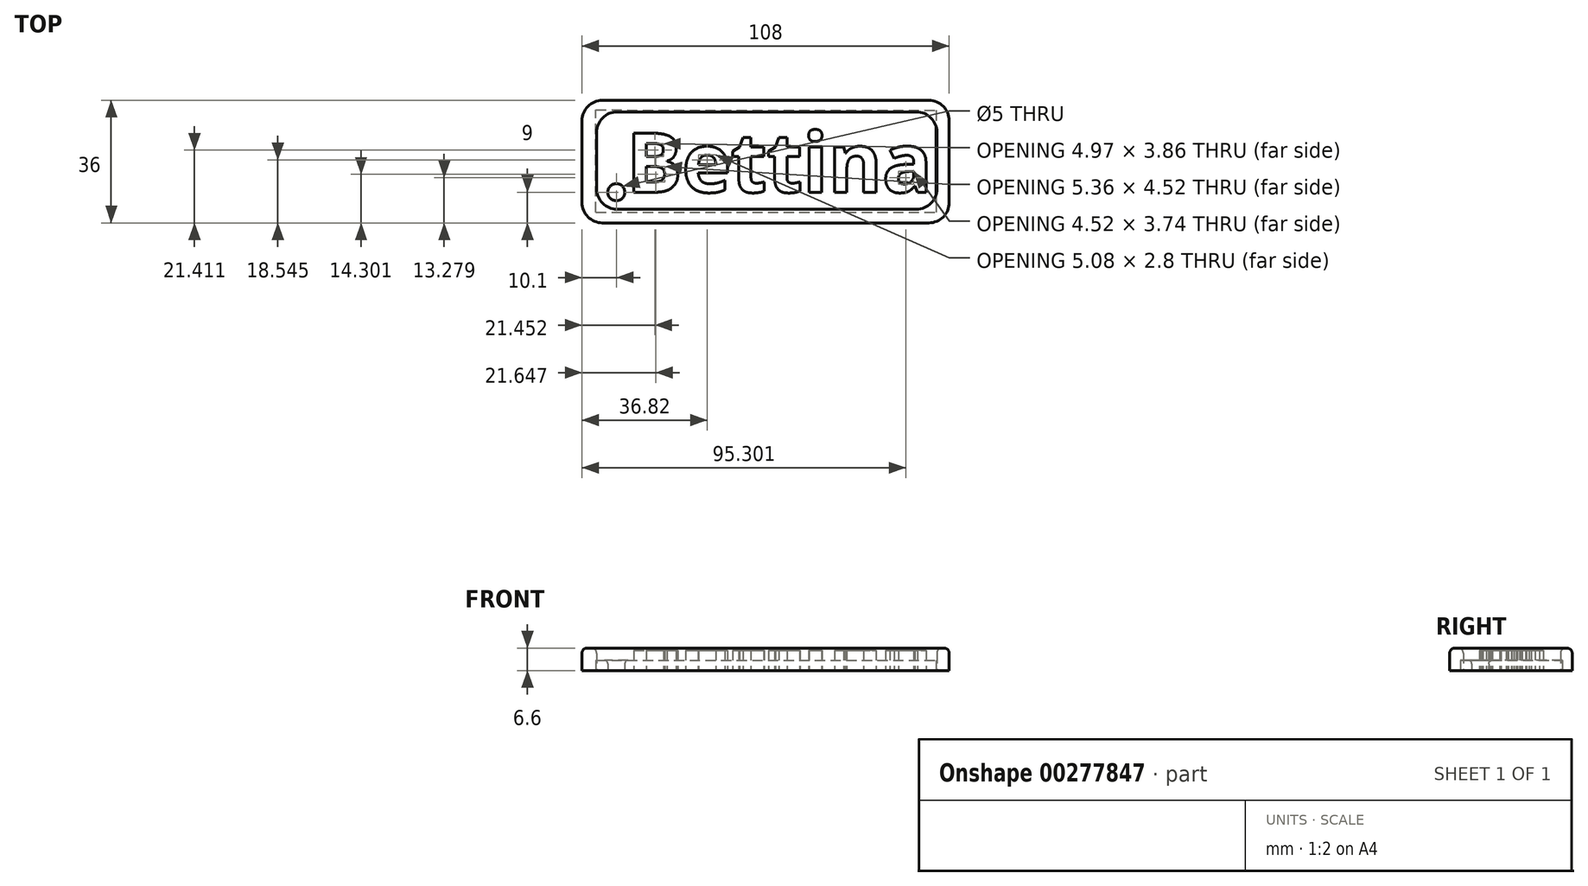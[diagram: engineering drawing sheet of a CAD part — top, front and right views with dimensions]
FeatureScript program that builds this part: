
annotation { "Feature Type Name" : "Feature", "Feature Type Description" : "" }
export const myFeature = defineFeature(function(context is Context, id is Id, definition is map)
    precondition{}
    {
        {
            var Q0;
            Q0=qCreatedBy(makeId("Top.planeOp"),FACE);
            var sketch = newSketch(context, id + "F0", { "sketchPlane" : qUnion([Q0])});
            skText(sketch, "E0", { "text": "Bettina", "fontName": "OpenSans-Bold.ttf"});
            const initialGuessF0  = {"E0": [0, 0, 1, 0, 0.02334]};
            skSetInitialGuess(sketch, initialGuessF0);
            skSolve(sketch);
        }
        {
            var Q0;
            Q0 = qSketchRegion(id + "F0", true);
            extrude(context, id + "F1", {"entities" : qUnion([Q0]), "depth" : 8 * mm});
        }
        {
            var Q0;
            Q0=makeQuery(id+"F1.opExtrude","SWEPT_BODY",BODY,{"disambiguationData":[OSD([sQuery(id+"F0.wireOp",EDGE,"E0.sketch_text.stroke-0"),sQuery(id+"F0.wireOp",EDGE,"E0.sketch_text.stroke-1"),sQuery(id+"F0.wireOp",EDGE,"E0.sketch_text.stroke-2"),sQuery(id+"F0.wireOp",EDGE,"E0.sketch_text.stroke-3"),sQuery(id+"F0.wireOp",EDGE,"E0.sketch_text.stroke-4"),sQuery(id+"F0.wireOp",EDGE,"E0.sketch_text.stroke-5"),sQuery(id+"F0.wireOp",EDGE,"E0.sketch_text.stroke-6"),sQuery(id+"F0.wireOp",EDGE,"E0.sketch_text.stroke-7"),sQuery(id+"F0.wireOp",EDGE,"E0.sketch_text.stroke-8"),sQuery(id+"F0.wireOp",EDGE,"E0.sketch_text.stroke-9"),sQuery(id+"F0.wireOp",EDGE,"E0.sketch_text.stroke-10"),sQuery(id+"F0.wireOp",EDGE,"E0.sketch_text.stroke-11"),sQuery(id+"F0.wireOp",EDGE,"E0.sketch_text.stroke-12"),sQuery(id+"F0.wireOp",EDGE,"E0.sketch_text.stroke-13"),sQuery(id+"F0.wireOp",EDGE,"E0.sketch_text.stroke-14"),sQuery(id+"F0.wireOp",EDGE,"E0.sketch_text.stroke-15"),sQuery(id+"F0.wireOp",EDGE,"E0.sketch_text.stroke-16"),sQuery(id+"F0.wireOp",EDGE,"E0.sketch_text.stroke-17"),sQuery(id+"F0.wireOp",EDGE,"E0.sketch_text.stroke-18"),sQuery(id+"F0.wireOp",EDGE,"E0.sketch_text.stroke-19"),sQuery(id+"F0.wireOp",EDGE,"E0.sketch_text.stroke-20"),sQuery(id+"F0.wireOp",EDGE,"E0.sketch_text.stroke-21"),sQuery(id+"F0.wireOp",EDGE,"E0.sketch_text.stroke-22"),sQuery(id+"F0.wireOp",EDGE,"E0.sketch_text.stroke-23"),sQuery(id+"F0.wireOp",EDGE,"E0.sketch_text.stroke-24")])]});
            var Q1;
            Q1=makeQuery(id+"F1.opExtrude","SWEPT_BODY",BODY,{"disambiguationData":[OSD([sQuery(id+"F0.wireOp",EDGE,"E0.sketch_text.stroke-25"),sQuery(id+"F0.wireOp",EDGE,"E0.sketch_text.stroke-26"),sQuery(id+"F0.wireOp",EDGE,"E0.sketch_text.stroke-27"),sQuery(id+"F0.wireOp",EDGE,"E0.sketch_text.stroke-28"),sQuery(id+"F0.wireOp",EDGE,"E0.sketch_text.stroke-29"),sQuery(id+"F0.wireOp",EDGE,"E0.sketch_text.stroke-30"),sQuery(id+"F0.wireOp",EDGE,"E0.sketch_text.stroke-31"),sQuery(id+"F0.wireOp",EDGE,"E0.sketch_text.stroke-32"),sQuery(id+"F0.wireOp",EDGE,"E0.sketch_text.stroke-33"),sQuery(id+"F0.wireOp",EDGE,"E0.sketch_text.stroke-34"),sQuery(id+"F0.wireOp",EDGE,"E0.sketch_text.stroke-35"),sQuery(id+"F0.wireOp",EDGE,"E0.sketch_text.stroke-36"),sQuery(id+"F0.wireOp",EDGE,"E0.sketch_text.stroke-37"),sQuery(id+"F0.wireOp",EDGE,"E0.sketch_text.stroke-38"),sQuery(id+"F0.wireOp",EDGE,"E0.sketch_text.stroke-39"),sQuery(id+"F0.wireOp",EDGE,"E0.sketch_text.stroke-40"),sQuery(id+"F0.wireOp",EDGE,"E0.sketch_text.stroke-41"),sQuery(id+"F0.wireOp",EDGE,"E0.sketch_text.stroke-42"),sQuery(id+"F0.wireOp",EDGE,"E0.sketch_text.stroke-43"),sQuery(id+"F0.wireOp",EDGE,"E0.sketch_text.stroke-44")])]});
            var Q2;
            Q2=makeQuery(id+"F1.opExtrude","SWEPT_BODY",BODY,{"disambiguationData":[OSD([sQuery(id+"F0.wireOp",EDGE,"E0.sketch_text.stroke-45"),sQuery(id+"F0.wireOp",EDGE,"E0.sketch_text.stroke-46"),sQuery(id+"F0.wireOp",EDGE,"E0.sketch_text.stroke-47"),sQuery(id+"F0.wireOp",EDGE,"E0.sketch_text.stroke-48"),sQuery(id+"F0.wireOp",EDGE,"E0.sketch_text.stroke-49"),sQuery(id+"F0.wireOp",EDGE,"E0.sketch_text.stroke-50"),sQuery(id+"F0.wireOp",EDGE,"E0.sketch_text.stroke-51"),sQuery(id+"F0.wireOp",EDGE,"E0.sketch_text.stroke-52"),sQuery(id+"F0.wireOp",EDGE,"E0.sketch_text.stroke-53"),sQuery(id+"F0.wireOp",EDGE,"E0.sketch_text.stroke-54"),sQuery(id+"F0.wireOp",EDGE,"E0.sketch_text.stroke-55"),sQuery(id+"F0.wireOp",EDGE,"E0.sketch_text.stroke-56"),sQuery(id+"F0.wireOp",EDGE,"E0.sketch_text.stroke-57"),sQuery(id+"F0.wireOp",EDGE,"E0.sketch_text.stroke-58"),sQuery(id+"F0.wireOp",EDGE,"E0.sketch_text.stroke-59"),sQuery(id+"F0.wireOp",EDGE,"E0.sketch_text.stroke-60"),sQuery(id+"F0.wireOp",EDGE,"E0.sketch_text.stroke-61"),sQuery(id+"F0.wireOp",EDGE,"E0.sketch_text.stroke-62")])]});
            var Q3;
            Q3=makeQuery(id+"F1.opExtrude","SWEPT_BODY",BODY,{"disambiguationData":[OSD([sQuery(id+"F0.wireOp",EDGE,"E0.sketch_text.stroke-63"),sQuery(id+"F0.wireOp",EDGE,"E0.sketch_text.stroke-64"),sQuery(id+"F0.wireOp",EDGE,"E0.sketch_text.stroke-65"),sQuery(id+"F0.wireOp",EDGE,"E0.sketch_text.stroke-66"),sQuery(id+"F0.wireOp",EDGE,"E0.sketch_text.stroke-67"),sQuery(id+"F0.wireOp",EDGE,"E0.sketch_text.stroke-68"),sQuery(id+"F0.wireOp",EDGE,"E0.sketch_text.stroke-69"),sQuery(id+"F0.wireOp",EDGE,"E0.sketch_text.stroke-70"),sQuery(id+"F0.wireOp",EDGE,"E0.sketch_text.stroke-71"),sQuery(id+"F0.wireOp",EDGE,"E0.sketch_text.stroke-72"),sQuery(id+"F0.wireOp",EDGE,"E0.sketch_text.stroke-73"),sQuery(id+"F0.wireOp",EDGE,"E0.sketch_text.stroke-74"),sQuery(id+"F0.wireOp",EDGE,"E0.sketch_text.stroke-75"),sQuery(id+"F0.wireOp",EDGE,"E0.sketch_text.stroke-76"),sQuery(id+"F0.wireOp",EDGE,"E0.sketch_text.stroke-77"),sQuery(id+"F0.wireOp",EDGE,"E0.sketch_text.stroke-78"),sQuery(id+"F0.wireOp",EDGE,"E0.sketch_text.stroke-79"),sQuery(id+"F0.wireOp",EDGE,"E0.sketch_text.stroke-80")])]});
            var Q4;
            Q4=makeQuery(id+"F1.opExtrude","SWEPT_BODY",BODY,{"disambiguationData":[OSD([sQuery(id+"F0.wireOp",EDGE,"E0.sketch_text.stroke-81"),sQuery(id+"F0.wireOp",EDGE,"E0.sketch_text.stroke-82"),sQuery(id+"F0.wireOp",EDGE,"E0.sketch_text.stroke-83"),sQuery(id+"F0.wireOp",EDGE,"E0.sketch_text.stroke-84"),sQuery(id+"F0.wireOp",EDGE,"E0.sketch_text.stroke-85")])]});
            var Q5;
            Q5=makeQuery(id+"F1.opExtrude","SWEPT_BODY",BODY,{"disambiguationData":[OSD([sQuery(id+"F0.wireOp",EDGE,"E0.sketch_text.stroke-86"),sQuery(id+"F0.wireOp",EDGE,"E0.sketch_text.stroke-87"),sQuery(id+"F0.wireOp",EDGE,"E0.sketch_text.stroke-88"),sQuery(id+"F0.wireOp",EDGE,"E0.sketch_text.stroke-89")])]});
            var Q6;
            Q6=makeQuery(id+"F1.opExtrude","SWEPT_BODY",BODY,{"disambiguationData":[OSD([sQuery(id+"F0.wireOp",EDGE,"E0.sketch_text.stroke-90"),sQuery(id+"F0.wireOp",EDGE,"E0.sketch_text.stroke-91"),sQuery(id+"F0.wireOp",EDGE,"E0.sketch_text.stroke-92"),sQuery(id+"F0.wireOp",EDGE,"E0.sketch_text.stroke-93"),sQuery(id+"F0.wireOp",EDGE,"E0.sketch_text.stroke-94"),sQuery(id+"F0.wireOp",EDGE,"E0.sketch_text.stroke-95"),sQuery(id+"F0.wireOp",EDGE,"E0.sketch_text.stroke-96"),sQuery(id+"F0.wireOp",EDGE,"E0.sketch_text.stroke-97"),sQuery(id+"F0.wireOp",EDGE,"E0.sketch_text.stroke-98"),sQuery(id+"F0.wireOp",EDGE,"E0.sketch_text.stroke-99"),sQuery(id+"F0.wireOp",EDGE,"E0.sketch_text.stroke-100"),sQuery(id+"F0.wireOp",EDGE,"E0.sketch_text.stroke-101"),sQuery(id+"F0.wireOp",EDGE,"E0.sketch_text.stroke-102"),sQuery(id+"F0.wireOp",EDGE,"E0.sketch_text.stroke-103"),sQuery(id+"F0.wireOp",EDGE,"E0.sketch_text.stroke-104"),sQuery(id+"F0.wireOp",EDGE,"E0.sketch_text.stroke-105"),sQuery(id+"F0.wireOp",EDGE,"E0.sketch_text.stroke-106")])]});
            var Q7;
            Q7=makeQuery(id+"F1.opExtrude","SWEPT_BODY",BODY,{"disambiguationData":[OSD([sQuery(id+"F0.wireOp",EDGE,"E0.sketch_text.stroke-107"),sQuery(id+"F0.wireOp",EDGE,"E0.sketch_text.stroke-108"),sQuery(id+"F0.wireOp",EDGE,"E0.sketch_text.stroke-109"),sQuery(id+"F0.wireOp",EDGE,"E0.sketch_text.stroke-110"),sQuery(id+"F0.wireOp",EDGE,"E0.sketch_text.stroke-111"),sQuery(id+"F0.wireOp",EDGE,"E0.sketch_text.stroke-112"),sQuery(id+"F0.wireOp",EDGE,"E0.sketch_text.stroke-113"),sQuery(id+"F0.wireOp",EDGE,"E0.sketch_text.stroke-114"),sQuery(id+"F0.wireOp",EDGE,"E0.sketch_text.stroke-115"),sQuery(id+"F0.wireOp",EDGE,"E0.sketch_text.stroke-116"),sQuery(id+"F0.wireOp",EDGE,"E0.sketch_text.stroke-117"),sQuery(id+"F0.wireOp",EDGE,"E0.sketch_text.stroke-118"),sQuery(id+"F0.wireOp",EDGE,"E0.sketch_text.stroke-119"),sQuery(id+"F0.wireOp",EDGE,"E0.sketch_text.stroke-120"),sQuery(id+"F0.wireOp",EDGE,"E0.sketch_text.stroke-121"),sQuery(id+"F0.wireOp",EDGE,"E0.sketch_text.stroke-122"),sQuery(id+"F0.wireOp",EDGE,"E0.sketch_text.stroke-123"),sQuery(id+"F0.wireOp",EDGE,"E0.sketch_text.stroke-124"),sQuery(id+"F0.wireOp",EDGE,"E0.sketch_text.stroke-125"),sQuery(id+"F0.wireOp",EDGE,"E0.sketch_text.stroke-126"),sQuery(id+"F0.wireOp",EDGE,"E0.sketch_text.stroke-127"),sQuery(id+"F0.wireOp",EDGE,"E0.sketch_text.stroke-128"),sQuery(id+"F0.wireOp",EDGE,"E0.sketch_text.stroke-129"),sQuery(id+"F0.wireOp",EDGE,"E0.sketch_text.stroke-130"),sQuery(id+"F0.wireOp",EDGE,"E0.sketch_text.stroke-131")])]});
            var Q8;
            Q8=qCreatedBy(makeId("Origin.pointOp"),VERTEX);
            transform(context, id + "F2", {"entities" : qUnion([Q0, Q1, Q2, Q3, Q4, Q5, Q6, Q7]), "transformType" : TransformType.SCALE_UNIFORMLY, "scale" : 0.75, "scalePoint" : qUnion([Q8]), "makeCopy" : false});
        }
        {
            var Q0;
            Q0=qCreatedBy(makeId("Top.planeOp"),FACE);
            var sketch = newSketch(context, id + "F3", { "sketchPlane" : qUnion([Q0])});
            skLineSegment(sketch, "E1", {"start": v(-4.79, -5) * mm, "end": v(95.21, -5) * mm});
            skLineSegment(sketch, "E2.bottom", {"start": v(-4.79, -5) * mm, "end": v(95.26, -5) * mm});
            skLineSegment(sketch, "E2.top", {"start": v(-4.79, 23.6) * mm, "end": v(95.26, 23.6) * mm});
            skLineSegment(sketch, "E2.left", {"start": v(-4.79, -5) * mm, "end": v(-4.79, 23.6) * mm});
            skLineSegment(sketch, "E2.right", {"start": v(95.26, -5) * mm, "end": v(95.26, 23.6) * mm});
            skLineSegment(sketch, "E3", {"start": v(-9.1, 27) * mm, "end": v(98.9, 27) * mm});
            skLineSegment(sketch, "E4", {"start": v(98.9, 27) * mm, "end": v(98.9, -9) * mm});
            skLineSegment(sketch, "E5", {"start": v(98.9, -9) * mm, "end": v(-9.1, -9) * mm});
            skLineSegment(sketch, "E6", {"start": v(-9.1, -9) * mm, "end": v(-9.1, 27) * mm});
            skSolve(sketch);
        }
        {
            var Q0;
            Q0 = qSketchRegion(id + "F3", true);
            extrude(context, id + "F4", {"entities" : qUnion([Q0]), "depth" : 6.6 * mm});
        }
        {
            var Q0;
            Q0=qCreatedBy(makeId("Top.planeOp"),FACE);
            var sketch = newSketch(context, id + "F5", { "sketchPlane" : qUnion([Q0])});
            skLineSegment(sketch, "E7", {"start": v(-5, -5.84) * mm, "end": v(-5, 24.16) * mm});
            skLineSegment(sketch, "E8", {"start": v(-5, 24.16) * mm, "end": v(95, 24.1) * mm});
            skLineSegment(sketch, "E9", {"start": v(95, 24.1) * mm, "end": v(94.98, -5.9) * mm});
            skLineSegment(sketch, "E10", {"start": v(-5, -5.84) * mm, "end": v(-5, -4) * mm});
            skLineSegment(sketch, "E11", {"start": v(-5, -5.84) * mm, "end": v(94.98, -5.9) * mm});
            skSolve(sketch);
        }
        {
            var Q0;
            Q0 = qSketchRegion(id + "F5", true);
            extrude(context, id + "F6", {"entities" : qUnion([Q0]), "depth" : 3 * mm});
        }
        {
            var Q0;
            Q0=makeQuery(id+"F4.opExtrude","SWEPT_EDGE",EDGE,{"disambiguationData":[OSD([sQuery(id+"F3.wireOp",EDGE,"E2.top"),sQuery(id+"F3.wireOp",EDGE,"E2.right")])]});
            var Q1;
            Q1=makeQuery(id+"F4.opExtrude","SWEPT_EDGE",EDGE,{"disambiguationData":[OSD([sQuery(id+"F3.wireOp",EDGE,"E2.bottom"),sQuery(id+"F3.wireOp",EDGE,"E2.right")])]});
            var Q2;
            Q2=makeQuery(id+"F4.opExtrude","SWEPT_EDGE",EDGE,{"disambiguationData":[OSD([sQuery(id+"F3.wireOp",EDGE,"E2.bottom"),sQuery(id+"F3.wireOp",EDGE,"E2.left")])]});
            var Q3;
            Q3=makeQuery(id+"F4.opExtrude","SWEPT_EDGE",EDGE,{"disambiguationData":[OSD([sQuery(id+"F3.wireOp",EDGE,"E2.top"),sQuery(id+"F3.wireOp",EDGE,"E2.left")])]});
            var Q4;
            Q4=makeQuery(id+"F4.opExtrude","SWEPT_EDGE",EDGE,{"disambiguationData":[OSD([sQuery(id+"F3.wireOp",EDGE,"E5"),sQuery(id+"F3.wireOp",EDGE,"E6")])]});
            var Q5;
            Q5=makeQuery(id+"F4.opExtrude","SWEPT_EDGE",EDGE,{"disambiguationData":[OSD([sQuery(id+"F3.wireOp",EDGE,"E3"),sQuery(id+"F3.wireOp",EDGE,"E6")])]});
            var Q6;
            Q6=makeQuery(id+"F4.opExtrude","SWEPT_EDGE",EDGE,{"disambiguationData":[OSD([sQuery(id+"F3.wireOp",EDGE,"E4"),sQuery(id+"F3.wireOp",EDGE,"E5")])]});
            var Q7;
            Q7=makeQuery(id+"F4.opExtrude","SWEPT_EDGE",EDGE,{"disambiguationData":[OSD([sQuery(id+"F3.wireOp",EDGE,"E3"),sQuery(id+"F3.wireOp",EDGE,"E4")])]});
            fillet(context, id + "F7", {"entities" : qUnion([Q0, Q1, Q2, Q3, Q4, Q5, Q6, Q7]), "radius" : 6 * mm, "tangentPropagation" : true, "allowEdgeOverflow" : false});
        }
        {
            var Q0;
            Q0=makeQuery(id+"F4.opExtrude","CAP_EDGE",EDGE,{"disambiguationData":[OSD([sQuery(id+"F3.wireOp",EDGE,"E5")])],"isStart":false});
            var Q1;
            Q1=makeQuery(id+"F4.opExtrude","CAP_EDGE",EDGE,{"disambiguationData":[OSD([sQuery(id+"F3.wireOp",EDGE,"E2.top")])],"isStart":false});
            fillet(context, id + "F8", {"entities" : qUnion([Q0, Q1]), "radius" : 1.5 * mm, "tangentPropagation" : true, "allowEdgeOverflow" : false});
        }
        {
            var Q0;
            Q0=makeQuery(id+"F4.opExtrude","SWEPT_BODY",BODY,{"disambiguationData":[OSD([sQuery(id+"F3.wireOp",EDGE,"E2.bottom"),sQuery(id+"F3.wireOp",EDGE,"E2.top"),sQuery(id+"F3.wireOp",EDGE,"E2.left"),sQuery(id+"F3.wireOp",EDGE,"E2.right"),sQuery(id+"F3.wireOp",EDGE,"E3"),sQuery(id+"F3.wireOp",EDGE,"E4"),sQuery(id+"F3.wireOp",EDGE,"E5"),sQuery(id+"F3.wireOp",EDGE,"E6")])]});
            var Q1;
            Q1=makeQuery(id+"F6.opExtrude","SWEPT_BODY",BODY,{"disambiguationData":[OSD([sQuery(id+"F5.wireOp",EDGE,"E7"),sQuery(id+"F5.wireOp",EDGE,"E8"),sQuery(id+"F5.wireOp",EDGE,"E9"),sQuery(id+"F5.wireOp",EDGE,"E10"),sQuery(id+"F5.wireOp",EDGE,"E11")])]});
            transform(context, id + "F9", {"entities" : qUnion([Q0, Q1]), "transformType" : TransformType.TRANSLATION_3D, "dx" : -4 * mm, "dy" : 0 * mm, "dz" : 0 * mm, "makeCopy" : false});
        }
        {
            var Q0;
            Q0=qCreatedBy(makeId("Top.planeOp"),FACE);
            var sketch = newSketch(context, id + "F10", { "sketchPlane" : qUnion([Q0])});
            skLineSegment(sketch, "E12", {"start": v(0, 0) * mm, "end": v(-3, 0) * mm});
            skCircle(sketch, "E13", {"center": v(-3, 0) * mm, "radius": 2.5 * mm});
            skSolve(sketch);
        }
        {
            var Q0;
            Q0 = qSketchRegion(id + "F10", true);
            extrude(context, id + "F11", {"entities" : qUnion([Q0]), "depth" : 25 * mm});
        }
        {
            var Q0;
            Q0=makeQuery(id+"F11.opExtrude","SWEPT_BODY",BODY,{"disambiguationData":[OSD([sQuery(id+"F10.wireOp",EDGE,"E13")])]});
            var Q1;
            Q1=makeQuery(id+"F6.opExtrude","SWEPT_BODY",BODY,{"disambiguationData":[OSD([sQuery(id+"F5.wireOp",EDGE,"E7"),sQuery(id+"F5.wireOp",EDGE,"E8"),sQuery(id+"F5.wireOp",EDGE,"E9"),sQuery(id+"F5.wireOp",EDGE,"E10"),sQuery(id+"F5.wireOp",EDGE,"E11")])]});
            booleanBodies(context, id + "F12", {"operationType" : BooleanOperationType.SUBTRACTION, "tools" : qUnion([Q0]), "targets" : qUnion([Q1])});
        }
        {
            var Q0;
            Q0=makeQuery(id+"F12.opBoolean","INTERSECT",EDGE,{"derivedFrom":[makeQuery(id+"F6.opExtrude","CAP_FACE",FACE,{"disambiguationData":[OSD([sQuery(id+"F5.wireOp",EDGE,"E7"),sQuery(id+"F5.wireOp",EDGE,"E8"),sQuery(id+"F5.wireOp",EDGE,"E9"),sQuery(id+"F5.wireOp",EDGE,"E10"),sQuery(id+"F5.wireOp",EDGE,"E11")])],"isStart":false}),makeQuery(id+"F11.opExtrude","SWEPT_FACE",FACE,{"disambiguationData":[OSD([sQuery(id+"F10.wireOp",EDGE,"E13")])]})]});
            fillet(context, id + "F13", {"entities" : qUnion([Q0]), "radius" : 1 * mm, "tangentPropagation" : true, "allowEdgeOverflow" : false});
        }
    });
